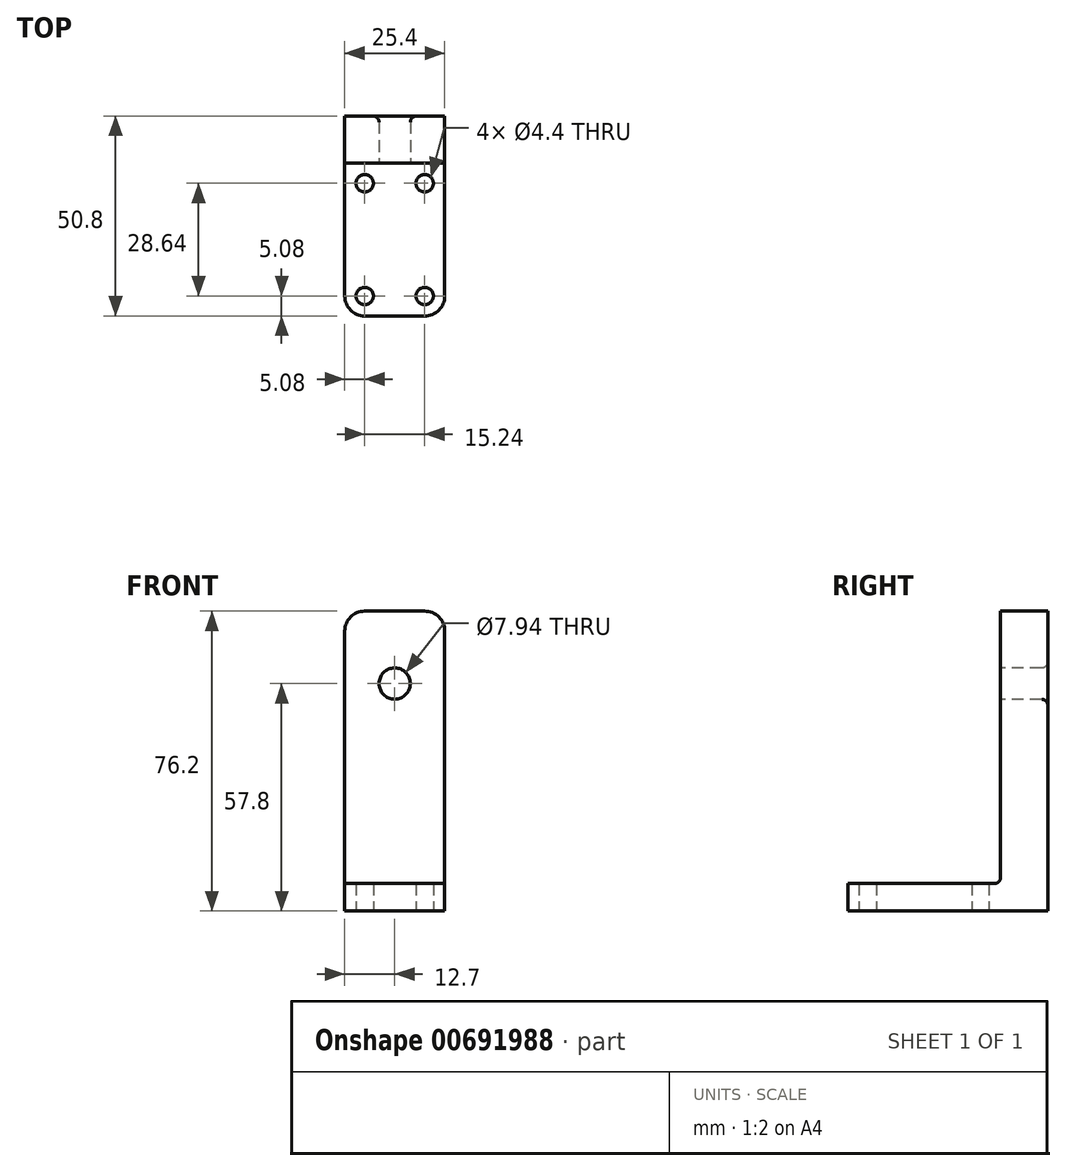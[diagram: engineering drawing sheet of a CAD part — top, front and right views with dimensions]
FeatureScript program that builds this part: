
annotation { "Feature Type Name" : "Feature", "Feature Type Description" : "" }
export const myFeature = defineFeature(function(context is Context, id is Id, definition is map)
    precondition{}
    {
        {
            var Q0;
            Q0=qCreatedBy(makeId("Right.planeOp"),FACE);
            var sketch = newSketch(context, id + "F0", { "sketchPlane" : qUnion([Q0])});
            skLineSegment(sketch, "E0", {"start": v(-50.8, 0) * mm, "end": v(-50.8, 7) * mm});
            skLineSegment(sketch, "E1", {"start": v(-50.8, 7) * mm, "end": v(-12, 7) * mm});
            skLineSegment(sketch, "E2", {"start": v(-12, 7) * mm, "end": v(-12, 76.2) * mm});
            skLineSegment(sketch, "E3", {"start": v(-12, 76.2) * mm, "end": v(0, 76.2) * mm});
            skLineSegment(sketch, "E4", {"start": v(0, 76.2) * mm, "end": v(0, 0) * mm});
            skLineSegment(sketch, "E5", {"start": v(-50.8, 0) * mm, "end": v(0, 0) * mm});
            skSolve(sketch);
        }
        {
            var Q0;
            Q0 = qSketchRegion(id + "F0", true);
            extrude(context, id + "F1", {"entities" : qUnion([Q0]), "depth" : 25.4 * mm, "offsetDistance" : 25.4 * mm});
        }
        {
            var Q0;
            Q0=makeQuery(id+"F1.opExtrude","SWEPT_FACE",FACE,{"disambiguationData":[OSD([sQuery(id+"F0.wireOp",EDGE,"E1")])]});
            var sketch = newSketch(context, id + "F2", { "sketchPlane" : qUnion([Q0])});
            skCircle(sketch, "E6", {"center": v(5.08, -45.72) * mm, "radius": 2 * mm});
            skCircle(sketch, "E7", {"center": v(5.08, -17.08) * mm, "radius": 2 * mm});
            skCircle(sketch, "E8", {"center": v(20.32, -17.08) * mm, "radius": 2 * mm});
            skCircle(sketch, "E9", {"center": v(20.32, -45.72) * mm, "radius": 2 * mm});
            skSolve(sketch);
        }
        {
            var Q0;
            Q0=sQuery(id+"F2.wireOp",VERTEX,"E8.center");
            var Q1;
            Q1=sQuery(id+"F2.wireOp",VERTEX,"E7.center");
            var Q2;
            Q2=sQuery(id+"F2.wireOp",VERTEX,"E6.center");
            var Q3;
            Q3=sQuery(id+"F2.wireOp",VERTEX,"E9.center");
            var Q4;
            Q4=makeQuery(id+"F1.opExtrude","SWEPT_BODY",BODY,{"disambiguationData":[OSD([sQuery(id+"F0.wireOp",EDGE,"E0"),sQuery(id+"F0.wireOp",EDGE,"E1"),sQuery(id+"F0.wireOp",EDGE,"E2"),sQuery(id+"F0.wireOp",EDGE,"E3"),sQuery(id+"F0.wireOp",EDGE,"E4"),sQuery(id+"F0.wireOp",EDGE,"E5")])]});
            hole(context, id + "F3", {"style" : HoleStyle.SIMPLE, "endStyle" : HoleEndStyle.THROUGH, "standardTappedOrClearance" : lookupTablePath({ "standard" : "ISO", "fit" : "Normal", "size" : "M4", "type" : "Clearance" }), "standardBlindInLast" : lookupTablePath({ "fit" : "Standard", "standard" : "ISO", "size" : "M4", "type" : "Clearance" }), "holeDiameter" : 4.4 * mm, "majorDiameter" : 6.35 * mm, "isTappedThrough" : true, "tappedDepth" : 12.7 * mm, "tapClearance" : 3, "locations" : qUnion([Q0, Q1, Q2, Q3]), "scope" : qUnion([Q4]), "startStyle" : HoleStartStyle.PART});
        }
        {
            var Q0;
            Q0=makeQuery(id+"F1.opExtrude","SWEPT_FACE",FACE,{"disambiguationData":[OSD([sQuery(id+"F0.wireOp",EDGE,"E2")])]});
            var sketch = newSketch(context, id + "F4", { "sketchPlane" : qUnion([Q0])});
            skCircle(sketch, "E10", {"center": v(12.7, 57.8) * mm, "radius": 3.97 * mm});
            skPoint(sketch, "E11", {"position": v(12.7, 76.2) * mm});
            skSolve(sketch);
        }
        {
            var Q0;
            Q0 = qSketchRegion(id + "F4", true);
            extrude(context, id + "F5", {"entities" : qUnion([Q0]), "operationType" : NewBodyOperationType.REMOVE, "oppositeDirection" : true, "depth" : 25.4 * mm, "offsetDistance" : 25.4 * mm});
        }
        {
            var Q0;
            Q0=makeQuery(id+"F1.opExtrude","CAP_EDGE",EDGE,{"disambiguationData":[OSD([sQuery(id+"F0.wireOp",EDGE,"E3")])],"isStart":false});
            var Q1;
            Q1=makeQuery(id+"F1.opExtrude","CAP_EDGE",EDGE,{"disambiguationData":[OSD([sQuery(id+"F0.wireOp",EDGE,"E3")])],"isStart":true});
            var Q2;
            Q2=makeQuery(id+"F1.opExtrude","CAP_EDGE",EDGE,{"disambiguationData":[OSD([sQuery(id+"F0.wireOp",EDGE,"E0")])],"isStart":false});
            var Q3;
            Q3=makeQuery(id+"F1.opExtrude","CAP_EDGE",EDGE,{"disambiguationData":[OSD([sQuery(id+"F0.wireOp",EDGE,"E0")])],"isStart":true});
            fillet(context, id + "F6", {"entities" : qUnion([Q0, Q1, Q2, Q3]), "radius" : 5.08 * mm, "tangentPropagation" : true, "allowEdgeOverflow" : false});
        }
        {
            var Q0;
            Q0=makeQuery(id+"F1.opExtrude","SWEPT_EDGE",EDGE,{"disambiguationData":[OSD([sQuery(id+"F0.wireOp",EDGE,"E1"),sQuery(id+"F0.wireOp",EDGE,"E2")])]});
            var Q1;
            Q1=makeQuery(id+"F5.boolean.opBoolean","COPY",EDGE,{"derivedFrom":makeQuery(id+"F5.opExtrude","CAP_EDGE",EDGE,{"disambiguationData":[OSD([sQuery(id+"F4.wireOp",EDGE,"E10")])],"isStart":true})});
            var Q2;
            Q2=makeQuery(id+"F5.boolean.opBoolean","INTERSECT",EDGE,{"derivedFrom":[makeQuery(id+"F1.opExtrude","SWEPT_FACE",FACE,{"disambiguationData":[OSD([sQuery(id+"F0.wireOp",EDGE,"E4")])]}),makeQuery(id+"F5.opExtrude","SWEPT_FACE",FACE,{"disambiguationData":[OSD([sQuery(id+"F4.wireOp",EDGE,"E10")])]})]});
            fillet(context, id + "F7", {"entities" : qUnion([Q0, Q1, Q2]), "radius" : 1.52 * mm, "tangentPropagation" : true, "allowEdgeOverflow" : false});
        }
    });
